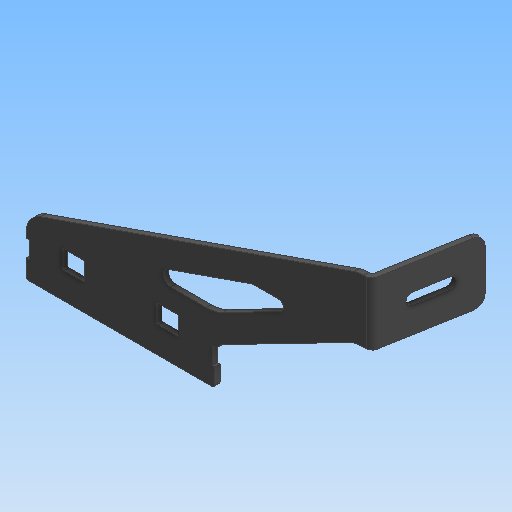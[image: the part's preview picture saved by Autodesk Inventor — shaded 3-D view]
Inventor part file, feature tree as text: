
AUTODESK INVENTOR PART (.ipt)
format: ipt  version: 2020 (Build 240168000, 168)  size: 405,504 bytes
history: native  units: mm
features: other x3, extrude x1, plane x1
ambient origin geometry x8: Origin, YZ Plane, XZ Plane, XY Plane, X Axis, Y Axis, Z Axis, Center Point
bodies: Body1 (feature_tree)
feature tree (5):
  other  "實體1"
  extrude  "擠出1"  Depth=130.0mm
  other  "折彎零件1"
  plane  "工作平面1"
  other  "定義1"
